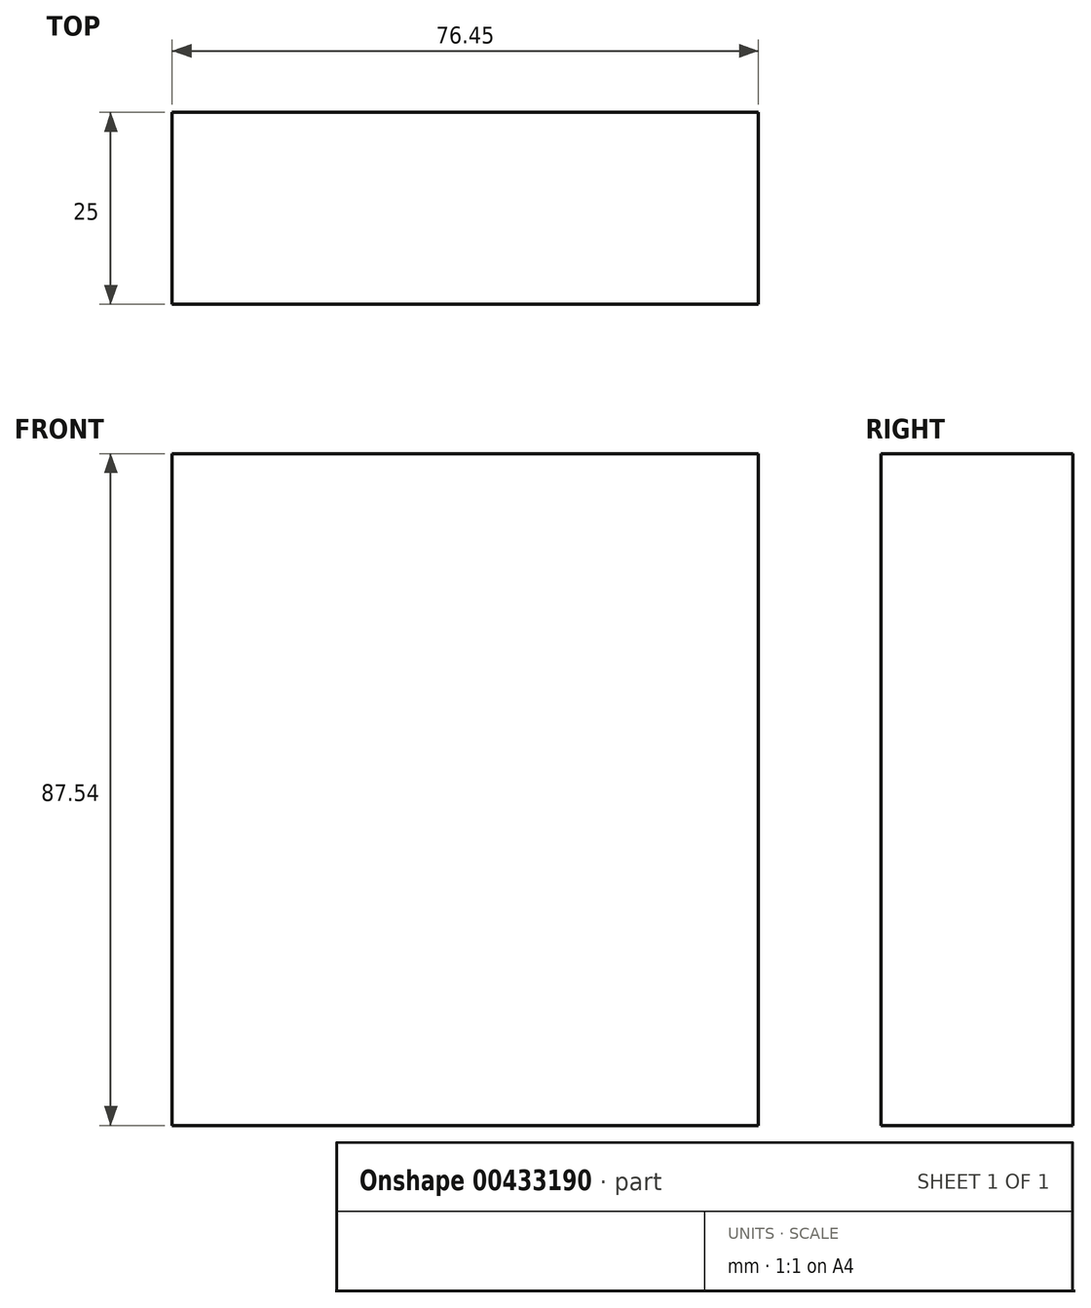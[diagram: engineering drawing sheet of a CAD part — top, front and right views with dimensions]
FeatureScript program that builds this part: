
annotation { "Feature Type Name" : "Feature", "Feature Type Description" : "" }
export const myFeature = defineFeature(function(context is Context, id is Id, definition is map)
    precondition{}
    {
        {
            var Q0;
            Q0=qCreatedBy(makeId("Front.planeOp"),FACE);
            var sketch = newSketch(context, id + "F0", { "sketchPlane" : qUnion([Q0])});
            skLineSegment(sketch, "E0.bottom", {"start": v(-124.98, 0) * mm, "end": v(-48.53, 0) * mm});
            skLineSegment(sketch, "E0.top", {"start": v(-124.98, 87.54) * mm, "end": v(-48.53, 87.54) * mm});
            skLineSegment(sketch, "E0.left", {"start": v(-124.98, 0) * mm, "end": v(-124.98, 87.54) * mm});
            skLineSegment(sketch, "E0.right", {"start": v(-48.53, 0) * mm, "end": v(-48.53, 87.54) * mm});
            skPoint(sketch, "E0.middle", {"position": v(-86.75, 43.77) * mm});
            skSolve(sketch);
        }
        {
            var Q0;
            Q0=makeQuery(id+"F0.imprint","IMPRINT",FACE,{"disambiguationData":[TD([[makeQuery(id+"F0.imprint","IMPRINT",EDGE,{"derivedFrom":sQuery(id+"F0.wireOp",EDGE,"E0.bottom")}),1.0]])]});
            extrude(context, id + "F1", {"entities" : qUnion([Q0]), "depth" : 25 * mm});
        }
    });
